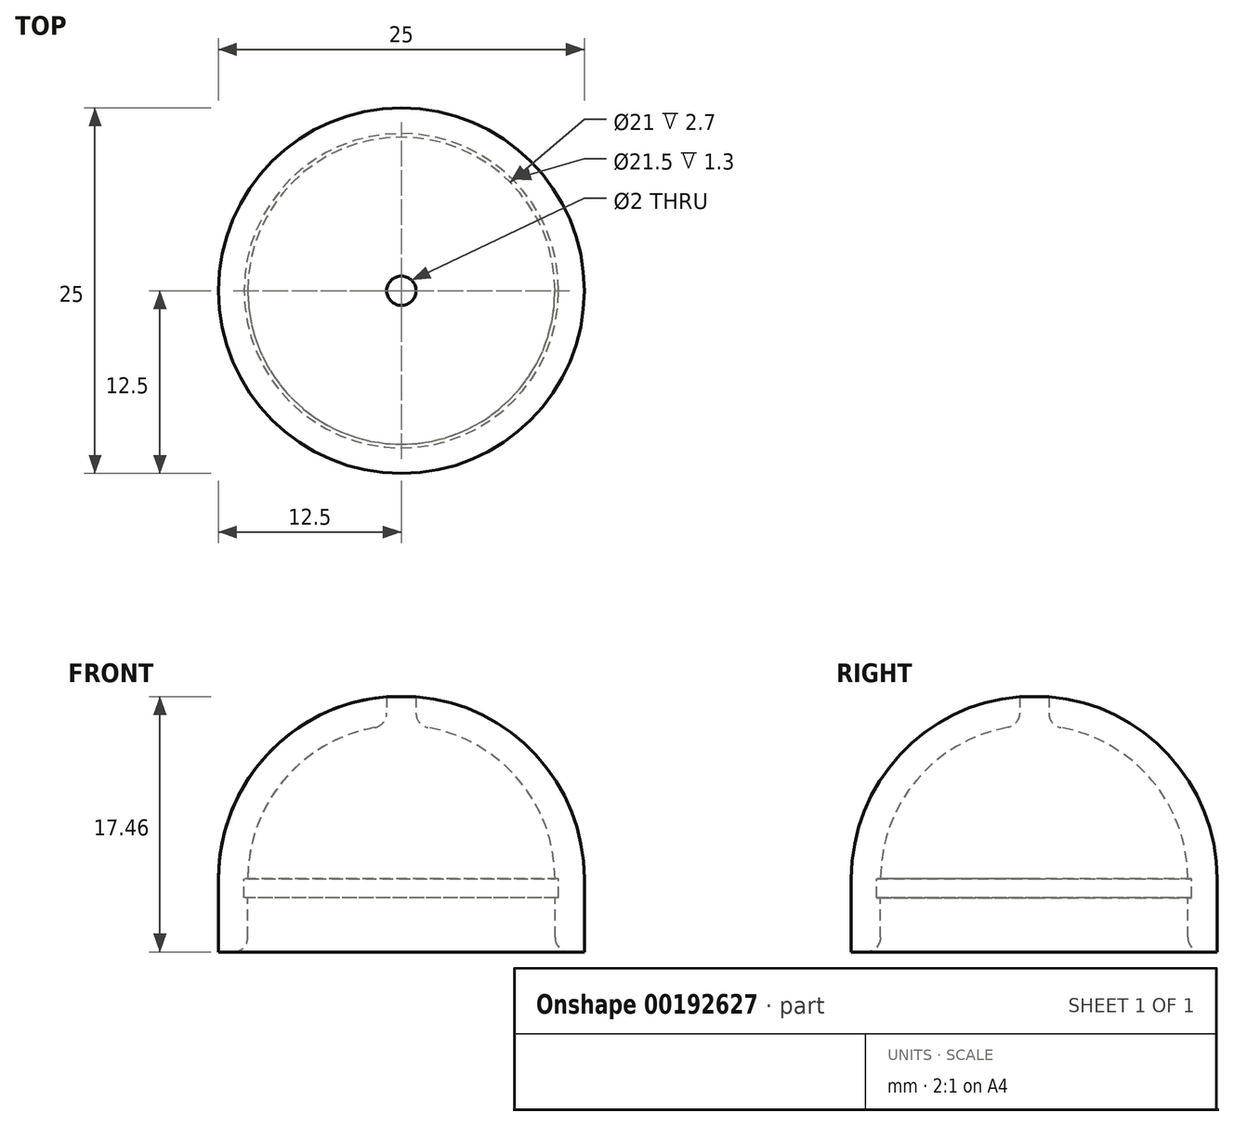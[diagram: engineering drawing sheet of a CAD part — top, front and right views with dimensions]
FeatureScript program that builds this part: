
annotation { "Feature Type Name" : "Feature", "Feature Type Description" : "" }
export const myFeature = defineFeature(function(context is Context, id is Id, definition is map)
    precondition{}
    {
        {
            var Q0;
            Q0=qCreatedBy(makeId("Front.planeOp"),FACE);
            var sketch = newSketch(context, id + "F0", { "sketchPlane" : qUnion([Q0])});
            skArc(sketch, "E0", {"start": v(0, 10.5) * mm, "mid": v(-7.42, 7.42) * mm, "end": v(-10.5, 0) * mm});
            skArc(sketch, "E1", {"start": v(0, 12.5) * mm, "mid": v(-8.84, 8.84) * mm, "end": v(-12.5, 0) * mm});
            skLineSegment(sketch, "E2", {"start": v(-10.5, 0) * mm, "end": v(-12.5, 0) * mm});
            skLineSegment(sketch, "E3", {"start": v(0, 10.5) * mm, "end": v(0, 12.5) * mm});
            skSolve(sketch);
        }
        {
            var Q0;
            Q0=qCreatedBy(makeId("Front.planeOp"),FACE);
            var sketch = newSketch(context, id + "F1", { "sketchPlane" : qUnion([Q0])});
            skLineSegment(sketch, "E4", {"start": v(0, 0) * mm, "end": v(0, 43.82) * mm});
            skSolve(sketch);
        }
        {
            var Q0;
            Q0=makeQuery(id+"F0.imprint","IMPRINT",FACE,{"disambiguationData":[TD([[makeQuery(id+"F0.imprint","IMPRINT",EDGE,{"derivedFrom":sQuery(id+"F0.wireOp",EDGE,"E0")}),-1.0]])]});
            var Q1;
            Q1=sQuery(id+"F1.wireOp",EDGE,"E4");
            revolve(context, id + "F2", {"entities" : qUnion([Q0]), "axis" : qUnion([Q1]), "revolveType" : RevolveType.FULL});
        }
        {
            var Q0;
            Q0=qCreatedBy(makeId("Top.planeOp"),FACE);
            var sketch = newSketch(context, id + "F3", { "sketchPlane" : qUnion([Q0])});
            skCircle(sketch, "E5", {"center": v(0, 0) * mm, "radius": 10.75 * mm});
            skSolve(sketch);
        }
        {
            var Q0;
            Q0=makeQuery(id+"F2.opRevolve","SWEPT_FACE",FACE,{"disambiguationData":[OSD([sQuery(id+"F0.wireOp",EDGE,"E2")])]});
            extrude(context, id + "F4", {"entities" : qUnion([Q0]), "operationType" : NewBodyOperationType.ADD, "depth" : 5 * mm});
        }
        {
            var Q0;
            Q0 = qSketchRegion(id + "F3", true);
            extrude(context, id + "F5", {"entities" : qUnion([Q0]), "operationType" : NewBodyOperationType.REMOVE, "oppositeDirection" : true, "depth" : 1.3 * mm});
        }
        {
            var Q0;
            Q0=qCreatedBy(makeId("Top.planeOp"),FACE);
            var sketch = newSketch(context, id + "F6", { "sketchPlane" : qUnion([Q0])});
            skCircle(sketch, "E6", {"center": v(0, 0) * mm, "radius": 1 * mm});
            skSolve(sketch);
        }
        {
            var Q0;
            Q0 = qSketchRegion(id + "F6", true);
            extrude(context, id + "F7", {"entities" : qUnion([Q0]), "operationType" : NewBodyOperationType.REMOVE, "depth" : 22.1 * mm});
        }
        {
            var Q0;
            Q0=makeQuery(id+"F4.opExtrude","CAP_EDGE",EDGE,{"disambiguationData":[OSD([sQuery(id+"F0.wireOp",EDGE,"E0"),sQuery(id+"F0.wireOp",EDGE,"E2")])],"isStart":false});
            var Q1;
            Q1=makeQuery(id+"F7.boolean.opBoolean","INTERSECT",EDGE,{"derivedFrom":[makeQuery(id+"F2.opRevolve","SWEPT_FACE",FACE,{"disambiguationData":[OSD([sQuery(id+"F0.wireOp",EDGE,"E0")])]}),makeQuery(id+"F7.opExtrude","SWEPT_FACE",FACE,{"disambiguationData":[OSD([sQuery(id+"F6.wireOp",EDGE,"E6")])]})]});
            fillet(context, id + "F8", {"entities" : qUnion([Q0, Q1]), "radius" : 1 * mm, "tangentPropagation" : true, "allowEdgeOverflow" : false});
        }
    });
